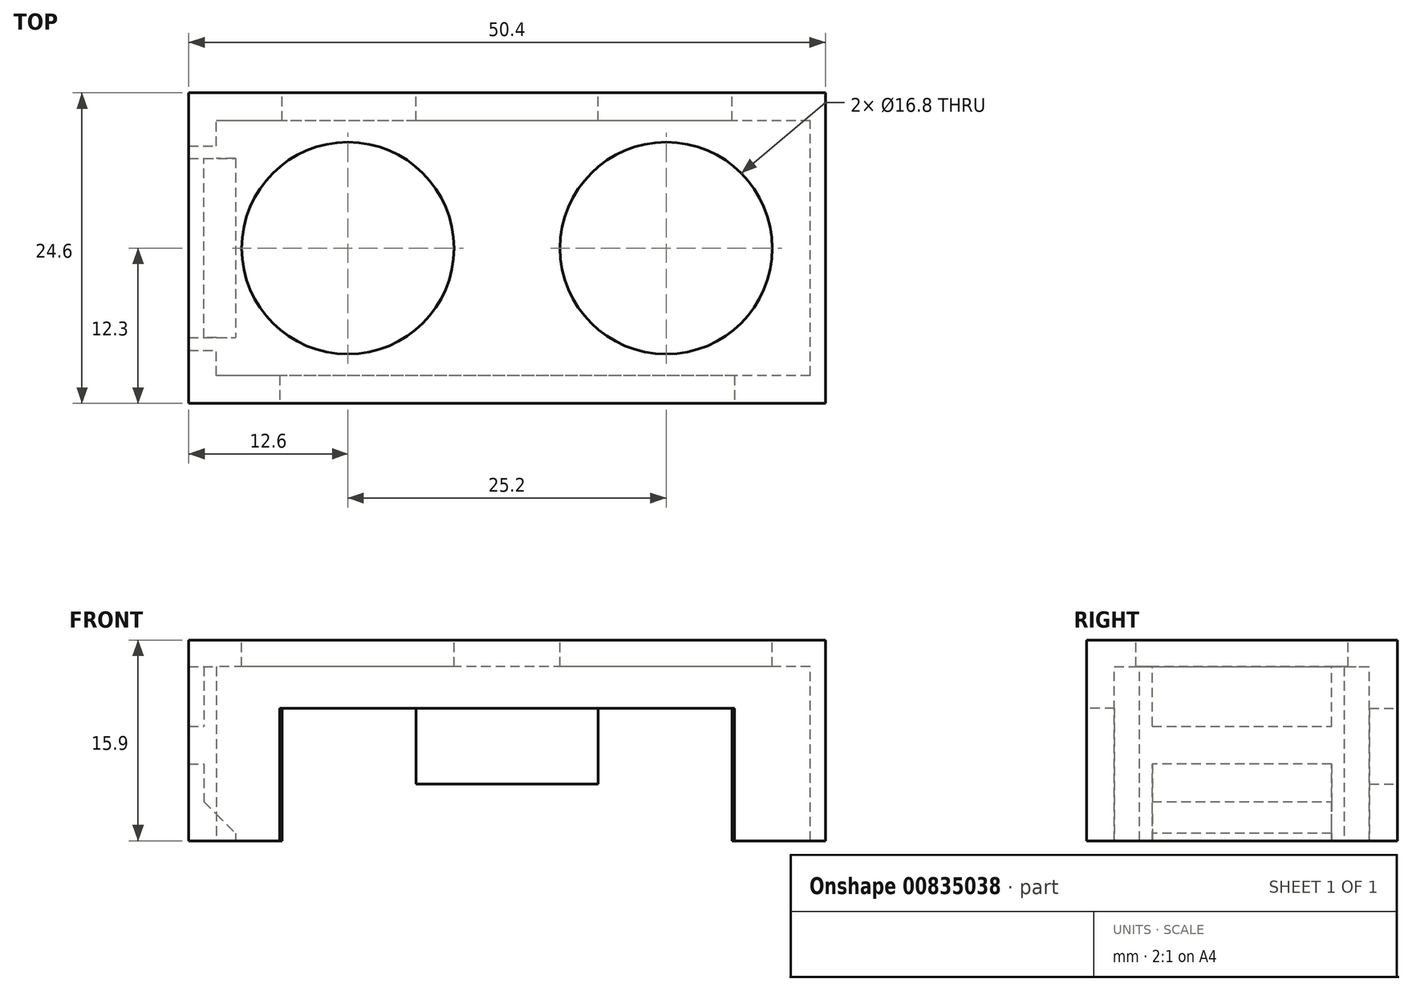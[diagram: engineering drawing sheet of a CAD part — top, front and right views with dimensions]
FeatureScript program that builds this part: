
annotation { "Feature Type Name" : "Feature", "Feature Type Description" : "" }
export const myFeature = defineFeature(function(context is Context, id is Id, definition is map)
    precondition{}
    {
        {
            var Q0;
            Q0=qCreatedBy(makeId("Top.planeOp"),FACE);
            var sketch = newSketch(context, id + "F0", { "sketchPlane" : qUnion([Q0])});
            skLineSegment(sketch, "E0.bottom", {"start": v(25.2, -12.3) * mm, "end": v(-25.2, -12.3) * mm});
            skLineSegment(sketch, "E0.top", {"start": v(25.2, 12.3) * mm, "end": v(-25.2, 12.3) * mm});
            skLineSegment(sketch, "E0.left", {"start": v(25.2, -12.3) * mm, "end": v(25.2, 12.3) * mm});
            skLineSegment(sketch, "E0.right", {"start": v(-25.2, -12.3) * mm, "end": v(-25.2, 12.3) * mm});
            skPoint(sketch, "E0.middle", {"position": v(0, 0) * mm});
            skLineSegment(sketch, "E1.bottom", {"start": v(23, -10.1) * mm, "end": v(-23, -10.1) * mm});
            skLineSegment(sketch, "E1.top", {"start": v(23, 10.1) * mm, "end": v(-23, 10.1) * mm});
            skLineSegment(sketch, "E1.left", {"start": v(23, -10.1) * mm, "end": v(23, 10.1) * mm});
            skLineSegment(sketch, "E1.right", {"start": v(-23, -10.1) * mm, "end": v(-23, 10.1) * mm});
            skSolve(sketch);
        }
        {
            var Q0;
            Q0=makeQuery(id+"F0.imprint","IMPRINT",FACE,{"disambiguationData":[TD([[makeQuery(id+"F0.imprint","IMPRINT",EDGE,{"derivedFrom":sQuery(id+"F0.wireOp",EDGE,"E0.bottom")}),-1.0]])]});
            var Q1;
            Q1=makeQuery(id+"F0.imprint","IMPRINT",FACE,{"disambiguationData":[TD([[makeQuery(id+"F0.imprint","IMPRINT",EDGE,{"derivedFrom":sQuery(id+"F0.wireOp",EDGE,"E1.bottom")}),-1.0]])]});
            extrude(context, id + "F1", {"entities" : qUnion([Q0, Q1]), "depth" : 2.1 * mm, "offsetDistance" : 25 * mm});
        }
        {
            var Q0;
            Q0=makeQuery(id+"F0.imprint","IMPRINT",FACE,{"disambiguationData":[TD([[makeQuery(id+"F0.imprint","IMPRINT",EDGE,{"derivedFrom":sQuery(id+"F0.wireOp",EDGE,"E0.bottom")}),-1.0]])]});
            extrude(context, id + "F2", {"entities" : qUnion([Q0]), "operationType" : NewBodyOperationType.ADD, "oppositeDirection" : true, "depth" : 13.8 * mm, "offsetDistance" : 25 * mm});
        }
        {
            var Q0;
            Q0=makeQuery(id+"F2.opExtrude","CAP_FACE",FACE,{"disambiguationData":[OSD([sQuery(id+"F0.wireOp",EDGE,"E0.bottom"),sQuery(id+"F0.wireOp",EDGE,"E0.top"),sQuery(id+"F0.wireOp",EDGE,"E0.left"),sQuery(id+"F0.wireOp",EDGE,"E0.right"),sQuery(id+"F0.wireOp",EDGE,"E1.bottom"),sQuery(id+"F0.wireOp",EDGE,"E1.top"),sQuery(id+"F0.wireOp",EDGE,"E1.left"),sQuery(id+"F0.wireOp",EDGE,"E1.right")])],"isStart":false});
            var sketch = newSketch(context, id + "F3", { "sketchPlane" : qUnion([Q0])});
            skLineSegment(sketch, "E2.bottom", {"start": v(-18, 10.1) * mm, "end": v(18, 10.1) * mm});
            skLineSegment(sketch, "E2.top", {"start": v(-18, 12.3) * mm, "end": v(18, 12.3) * mm});
            skLineSegment(sketch, "E2.left", {"start": v(-18, 10.1) * mm, "end": v(-18, 12.3) * mm});
            skLineSegment(sketch, "E2.right", {"start": v(18, 10.1) * mm, "end": v(18, 12.3) * mm});
            skPoint(sketch, "E2.middle", {"position": v(0, 11.2) * mm});
            skSolve(sketch);
        }
        {
            var Q0;
            Q0 = qSketchRegion(id + "F3", true);
            extrude(context, id + "F4", {"entities" : qUnion([Q0]), "operationType" : NewBodyOperationType.REMOVE, "oppositeDirection" : true, "depth" : 10.5 * mm, "offsetDistance" : 25 * mm});
        }
        {
            var Q0;
            Q0=makeQuery(id+"F1.opExtrude","CAP_FACE",FACE,{"disambiguationData":[OSD([sQuery(id+"F0.wireOp",EDGE,"E0.bottom"),sQuery(id+"F0.wireOp",EDGE,"E0.top"),sQuery(id+"F0.wireOp",EDGE,"E0.left"),sQuery(id+"F0.wireOp",EDGE,"E0.right")])],"isStart":false});
            var sketch = newSketch(context, id + "F5", { "sketchPlane" : qUnion([Q0])});
            skCircle(sketch, "E3", {"center": v(-12.6, 0) * mm, "radius": 8.4 * mm});
            skCircle(sketch, "E4", {"center": v(12.6, 0) * mm, "radius": 8.4 * mm});
            skPoint(sketch, "E5", {"position": v(25.2, 0) * mm});
            skSolve(sketch);
        }
        {
            var Q0;
            Q0=makeQuery(id+"F5.imprint","IMPRINT",FACE,{"disambiguationData":[TD([[makeQuery(id+"F5.imprint","IMPRINT",EDGE,{"derivedFrom":sQuery(id+"F5.wireOp",EDGE,"E4")}),1.0]])]});
            var Q1;
            Q1=makeQuery(id+"F5.imprint","IMPRINT",FACE,{"disambiguationData":[TD([[makeQuery(id+"F5.imprint","IMPRINT",EDGE,{"derivedFrom":sQuery(id+"F5.wireOp",EDGE,"E3")}),1.0]])]});
            extrude(context, id + "F6", {"entities" : qUnion([Q0, Q1]), "operationType" : NewBodyOperationType.REMOVE, "oppositeDirection" : true, "depth" : 25 * mm, "offsetDistance" : 25 * mm});
        }
        {
            var Q0;
            Q0=makeQuery(id+"F2.opExtrude","CAP_FACE",FACE,{"disambiguationData":[OSD([sQuery(id+"F0.wireOp",EDGE,"E0.bottom"),sQuery(id+"F0.wireOp",EDGE,"E0.top"),sQuery(id+"F0.wireOp",EDGE,"E0.left"),sQuery(id+"F0.wireOp",EDGE,"E0.right"),sQuery(id+"F0.wireOp",EDGE,"E1.bottom"),sQuery(id+"F0.wireOp",EDGE,"E1.top"),sQuery(id+"F0.wireOp",EDGE,"E1.left"),sQuery(id+"F0.wireOp",EDGE,"E1.right")])],"isStart":false});
            var sketch = newSketch(context, id + "F7", { "sketchPlane" : qUnion([Q0])});
            skLineSegment(sketch, "E6.bottom", {"start": v(-17.8, -10.1) * mm, "end": v(-7.2, -10.1) * mm});
            skLineSegment(sketch, "E6.top", {"start": v(-17.8, -12.3) * mm, "end": v(-7.2, -12.3) * mm});
            skLineSegment(sketch, "E6.left", {"start": v(-17.8, -10.1) * mm, "end": v(-17.8, -12.3) * mm});
            skLineSegment(sketch, "E6.right", {"start": v(-7.2, -10.1) * mm, "end": v(-7.2, -12.3) * mm});
            skLineSegment(sketch, "E7.bottom", {"start": v(7.2, -10.1) * mm, "end": v(17.8, -10.1) * mm});
            skLineSegment(sketch, "E7.top", {"start": v(7.2, -12.3) * mm, "end": v(17.8, -12.3) * mm});
            skLineSegment(sketch, "E7.left", {"start": v(7.2, -10.1) * mm, "end": v(7.2, -12.3) * mm});
            skLineSegment(sketch, "E7.right", {"start": v(17.8, -10.1) * mm, "end": v(17.8, -12.3) * mm});
            skSolve(sketch);
        }
        {
            var Q0;
            Q0=makeQuery(id+"F7.imprint","IMPRINT",FACE,{"disambiguationData":[TD([[makeQuery(id+"F7.imprint","IMPRINT",EDGE,{"derivedFrom":sQuery(id+"F7.wireOp",EDGE,"E6.bottom")}),1.0]])]});
            var Q1;
            Q1=makeQuery(id+"F7.imprint","IMPRINT",FACE,{"disambiguationData":[TD([[makeQuery(id+"F7.imprint","IMPRINT",EDGE,{"derivedFrom":sQuery(id+"F7.wireOp",EDGE,"E7.bottom")}),1.0]])]});
            extrude(context, id + "F8", {"entities" : qUnion([Q0, Q1]), "operationType" : NewBodyOperationType.REMOVE, "oppositeDirection" : true, "depth" : 10.5 * mm, "offsetDistance" : 25 * mm});
        }
        {
            var Q0;
            {var subQ0=sQuery(id+"F0.wireOp",EDGE,"E0.top");var subQ1=sQuery(id+"F0.wireOp",EDGE,"E1.top");Q0=makeQuery(id+"F8.boolean.opBoolean","SPLIT",FACE,{"disambiguationData":[TD([makeQuery(id+"F8.opExtrude","SWEPT_FACE",FACE,{"disambiguationData":[OSD([sQuery(id+"F7.wireOp",EDGE,"E6.right")])]})])],"derivedFrom":makeQuery(id+"F2.opExtrude","CAP_FACE",FACE,{"disambiguationData":[OSD([sQuery(id+"F0.wireOp",EDGE,"E0.bottom"),subQ0,sQuery(id+"F0.wireOp",EDGE,"E0.left"),sQuery(id+"F0.wireOp",EDGE,"E0.right"),sQuery(id+"F0.wireOp",EDGE,"E1.bottom"),subQ1,sQuery(id+"F0.wireOp",EDGE,"E1.left"),sQuery(id+"F0.wireOp",EDGE,"E1.right")])],"isStart":false})});}
            extrude(context, id + "F9", {"entities" : qUnion([Q0]), "operationType" : NewBodyOperationType.REMOVE, "oppositeDirection" : true, "depth" : 4.5 * mm, "offsetDistance" : 25 * mm});
        }
        {
            var Q0;
            Q0=makeQuery(id+"F2.opExtrude","SWEPT_FACE",FACE,{"disambiguationData":[OSD([sQuery(id+"F0.wireOp",EDGE,"E1.right")])]});
            var sketch = newSketch(context, id + "F10", { "sketchPlane" : qUnion([Q0])});
            skLineSegment(sketch, "E8.bottom", {"start": v(-8.1, 0) * mm, "end": v(-7.1, 0) * mm});
            skLineSegment(sketch, "E8.top", {"start": v(-8.1, -13.8) * mm, "end": v(-7.1, -13.8) * mm});
            skLineSegment(sketch, "E8.left", {"start": v(-8.1, 0) * mm, "end": v(-8.1, -13.8) * mm});
            skLineSegment(sketch, "E8.right", {"start": v(-7.1, 0) * mm, "end": v(-7.1, -13.8) * mm});
            skLineSegment(sketch, "E9.MirrorCS", {"start": v(8.1, 0) * mm, "end": v(8.1, -13.8) * mm});
            skLineSegment(sketch, "E10.MirrorCS", {"start": v(8.1, -13.8) * mm, "end": v(7.1, -13.8) * mm});
            skLineSegment(sketch, "E11.MirrorCS", {"start": v(7.1, 0) * mm, "end": v(7.1, -13.8) * mm});
            skLineSegment(sketch, "E12.MirrorCS", {"start": v(8.1, 0) * mm, "end": v(7.1, 0) * mm});
            skSolve(sketch);
        }
        {
            var Q0;
            Q0=makeQuery(id+"F10.imprint","IMPRINT",FACE,{"disambiguationData":[TD([[makeQuery(id+"F10.imprint","IMPRINT",EDGE,{"derivedFrom":sQuery(id+"F10.wireOp",EDGE,"E8.bottom")}),-1.0]])]});
            var Q1;
            Q1=makeQuery(id+"F10.imprint","IMPRINT",FACE,{"disambiguationData":[TD([[makeQuery(id+"F10.imprint","IMPRINT",EDGE,{"derivedFrom":sQuery(id+"F10.wireOp",EDGE,"E9.MirrorCS")}),-1.0]])]});
            extrude(context, id + "F11", {"entities" : qUnion([Q0, Q1]), "operationType" : NewBodyOperationType.REMOVE, "oppositeDirection" : true, "depth" : 25 * mm, "offsetDistance" : 25 * mm});
        }
        {
            var Q0;
            {var subQ0=sQuery(id+"F0.wireOp",EDGE,"E1.right");Q0=makeQuery(id+"F11.boolean.opBoolean","SPLIT",FACE,{"disambiguationData":[TD([makeQuery(id+"F11.opExtrude","SWEPT_FACE",FACE,{"disambiguationData":[OSD([sQuery(id+"F10.wireOp",EDGE,"E8.right")])]})])],"derivedFrom":makeQuery(id+"F2.opExtrude","SWEPT_FACE",FACE,{"disambiguationData":[OSD([subQ0])]})});}
            var sketch = newSketch(context, id + "F12", { "sketchPlane" : qUnion([Q0])});
            skLineSegment(sketch, "E13.bottom", {"start": v(-7.1, -13.8) * mm, "end": v(7.1, -13.8) * mm});
            skLineSegment(sketch, "E13.top", {"start": v(-7.1, -11.7) * mm, "end": v(7.1, -11.7) * mm});
            skLineSegment(sketch, "E13.left", {"start": v(-7.1, -13.8) * mm, "end": v(-7.1, -11.7) * mm});
            skLineSegment(sketch, "E13.right", {"start": v(7.1, -13.8) * mm, "end": v(7.1, -11.7) * mm});
            skSolve(sketch);
        }
        {
            var Q0;
            Q0=makeQuery(id+"F12.imprint","IMPRINT",FACE,{"disambiguationData":[TD([[makeQuery(id+"F12.imprint","IMPRINT",EDGE,{"derivedFrom":sQuery(id+"F12.wireOp",EDGE,"E13.bottom")}),1.0]])]});
            extrude(context, id + "F13", {"entities" : qUnion([Q0]), "operationType" : NewBodyOperationType.ADD, "depth" : 1.5 * mm, "offsetDistance" : 25 * mm});
        }
        {
            var Q0;
            Q0=makeQuery(id+"F13.opExtrude","CAP_EDGE",EDGE,{"disambiguationData":[OSD([sQuery(id+"F12.wireOp",EDGE,"E13.top")])],"isStart":false});
            chamfer(context, id + "F14", {"entities" : qUnion([Q0]), "width" : 1.5 * mm, "tangentPropagation" : true});
        }
        {
            var Q0;
            {var subQ0=sQuery(id+"F0.wireOp",EDGE,"E1.left");Q0=makeQuery(id+"FjfDs8jOAe0jGOs_1.1.F11.boolean.opBoolean","SPLIT",FACE,{"disambiguationData":[TD([makeQuery(id+"FjfDs8jOAe0jGOs_1.1.F11.opExtrude","SWEPT_FACE",FACE,{"disambiguationData":[OSD([sQuery(id+"F10.wireOp",EDGE,"E8.right")])]})])],"derivedFrom":makeQuery(id+"F2.opExtrude","SWEPT_FACE",FACE,{"disambiguationData":[OSD([subQ0])]})});}
            extrude(context, id + "F15", {"entities" : qUnion([Q0]), "operationType" : NewBodyOperationType.REMOVE, "oppositeDirection" : true, "depth" : 1 * mm, "offsetDistance" : 25 * mm});
        }
        {
            var Q0;
            {var subQ0=sQuery(id+"F0.wireOp",EDGE,"E1.right");Q0=makeQuery(id+"F11.boolean.opBoolean","SPLIT",FACE,{"disambiguationData":[TD([makeQuery(id+"F11.opExtrude","SWEPT_FACE",FACE,{"disambiguationData":[OSD([sQuery(id+"F10.wireOp",EDGE,"E8.right")])]})])],"derivedFrom":makeQuery(id+"F2.opExtrude","SWEPT_FACE",FACE,{"disambiguationData":[OSD([subQ0])]})});}
            extrude(context, id + "F16", {"entities" : qUnion([Q0]), "operationType" : NewBodyOperationType.REMOVE, "oppositeDirection" : true, "depth" : 1 * mm, "offsetDistance" : 25 * mm});
        }
        {
            var Q0;
            {var subQ0=sQuery(id+"F0.wireOp",EDGE,"E1.left");Q0=makeQuery(id+"FjfDs8jOAe0jGOs_1.1.F11.boolean.opBoolean","SPLIT",EDGE,{"disambiguationData":[TD([makeQuery(id+"FjfDs8jOAe0jGOs_1.1.F11.opExtrude","SWEPT_FACE",FACE,{"disambiguationData":[OSD([sQuery(id+"F10.wireOp",EDGE,"E8.right")])]})])],"derivedFrom":makeQuery(id+"F2.opExtrude","CAP_EDGE",EDGE,{"disambiguationData":[OSD([subQ0])],"isStart":true})});}
            var Q1;
            Q1=makeQuery(id+"F16.boolean.opBoolean","COPY",EDGE,{"derivedFrom":makeQuery(id+"F16.opExtrude","CAP_EDGE",EDGE,{"disambiguationData":[OSD([sQuery(id+"F0.wireOp",EDGE,"E1.right")])],"isStart":false})});
            var Q2;
            Q2=makeQuery(id+"F15.boolean.opBoolean","COPY",EDGE,{"derivedFrom":makeQuery(id+"F15.opExtrude","CAP_EDGE",EDGE,{"disambiguationData":[OSD([sQuery(id+"F0.wireOp",EDGE,"E1.left")])],"isStart":false})});
            chamfer(context, id + "F17", {"entities" : qUnion([Q0, Q1, Q2]), "width" : 1 * mm, "tangentPropagation" : true});
        }
        {
            var Q0;
            Q0=makeQuery(id+"F16.boolean.opBoolean","COPY",FACE,{"derivedFrom":makeQuery(id+"F16.opExtrude","CAP_FACE",FACE,{"disambiguationData":[OSD([sQuery(id+"F0.wireOp",EDGE,"E1.right")])],"isStart":false})});
            var sketch = newSketch(context, id + "F18", { "sketchPlane" : qUnion([Q0])});
            skLineSegment(sketch, "E14.bottom", {"start": v(7.1, -7.72) * mm, "end": v(-7.1, -7.72) * mm});
            skLineSegment(sketch, "E14.top", {"start": v(7.1, -4.72) * mm, "end": v(-7.1, -4.72) * mm});
            skLineSegment(sketch, "E14.left", {"start": v(7.1, -7.72) * mm, "end": v(7.1, -4.72) * mm});
            skLineSegment(sketch, "E14.right", {"start": v(-7.1, -7.72) * mm, "end": v(-7.1, -4.72) * mm});
            skSolve(sketch);
        }
        {
            var Q0;
            Q0=makeQuery(id+"F18.imprint","IMPRINT",FACE,{"disambiguationData":[TD([[makeQuery(id+"F18.imprint","IMPRINT",EDGE,{"derivedFrom":sQuery(id+"F18.wireOp",EDGE,"E14.bottom")}),-1.0]])]});
            extrude(context, id + "F19", {"entities" : qUnion([Q0]), "operationType" : NewBodyOperationType.REMOVE, "oppositeDirection" : true, "depth" : 25 * mm, "offsetDistance" : 25 * mm});
        }
        {
            var Q0;
            Q0=makeQuery(id+"F19.boolean.opBoolean","SPLIT",BODY,{"disambiguationData":[OD(1.0)],"derivedFrom":makeQuery(id+"F1.opExtrude","SWEPT_BODY",BODY,{"disambiguationData":[OSD([sQuery(id+"F0.wireOp",EDGE,"E0.bottom"),sQuery(id+"F0.wireOp",EDGE,"E0.top"),sQuery(id+"F0.wireOp",EDGE,"E0.left"),sQuery(id+"F0.wireOp",EDGE,"E0.right")])]})});
            var Q1;
            Q1=makeQuery(id+"F19.boolean.opBoolean","COPY",FACE,{"derivedFrom":makeQuery(id+"F19.opExtrude","SWEPT_FACE",FACE,{"disambiguationData":[OSD([sQuery(id+"F18.wireOp",EDGE,"E14.top")])]})});
            transform(context, id + "F20", {"entities" : qUnion([Q0]), "transformType" : TransformType.TRANSLATION_DISTANCE, "transformDirection" : qUnion([Q1]), "distance" : 3 * mm, "oppositeDirection" : true, "makeCopy" : false});
        }
        {
            var Q0;
            Q0=makeQuery(id+"F19.boolean.opBoolean","SPLIT",BODY,{"disambiguationData":[OD(0.0)],"derivedFrom":makeQuery(id+"F1.opExtrude","SWEPT_BODY",BODY,{"disambiguationData":[OSD([sQuery(id+"F0.wireOp",EDGE,"E0.bottom"),sQuery(id+"F0.wireOp",EDGE,"E0.top"),sQuery(id+"F0.wireOp",EDGE,"E0.left"),sQuery(id+"F0.wireOp",EDGE,"E0.right")])]})});
            var Q1;
            Q1=makeQuery(id+"F19.boolean.opBoolean","SPLIT",BODY,{"disambiguationData":[OD(1.0)],"derivedFrom":makeQuery(id+"F1.opExtrude","SWEPT_BODY",BODY,{"disambiguationData":[OSD([sQuery(id+"F0.wireOp",EDGE,"E0.bottom"),sQuery(id+"F0.wireOp",EDGE,"E0.top"),sQuery(id+"F0.wireOp",EDGE,"E0.left"),sQuery(id+"F0.wireOp",EDGE,"E0.right")])]})});
            booleanBodies(context, id + "F21", {"operationType" : BooleanOperationType.UNION, "tools" : qUnion([Q0, Q1])});
        }
    });
